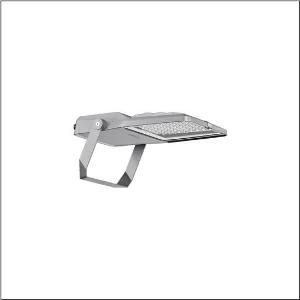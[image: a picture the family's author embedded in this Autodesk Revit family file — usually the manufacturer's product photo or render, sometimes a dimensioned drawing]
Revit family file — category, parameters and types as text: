
# Revit family: floodlight_fl_21_mini___pl52_5xa7775d2d1a_5239
name_source: partatom
category: Lighting Fixtures
units: mm (PartAtom-declared; Revit-internal decimal feet)

## family parameters
Cut with Voids When Loaded = No
Host = Face
Light Source = No
Part Type = Normal
Room Calculation Point = No
Round Connector Dimension = Use Diameter
Shared = No

## types (1)
- --- (1 x LED, 17840 lm, 142.9 W, 3000K)
    Apparent Load = 143 VA
    CIE Flux Codes = 26 60 98 100 100
    Color Rendering = 70
    Color Temperature = 3000K
    Default Elevation = 1800 mm
    Description = Floodlight FL 21 mini, floodlight, primary light control with lens, of PMMA, primary optical cover: protective disc, of toughened safety glass, transparent, light distribution: PL52, light emission: direct distribution, installation type: surface-mounted, LED, High Power LED, rated luminous flux: 17.840lm, luminous efficacy: 125lm/W, light colour: 730, colour temperature: 3000K, control gear: Smart Interface (Zhaga), control: flexible luminous flux parameterisation, time-dependent luminous flux control, constant luminous flux control, overheat protection, pre-setting: logarithmic dimming characteristic, with terminal, 6-pole, mains connection: 220..240V, AC, 50/60Hz, start of lifetime: 143W, end of service life: 151W, reduction: 63W, luminaire housing, of diecast aluminium, powder-coated, SITECO metallic grey (DB 702S), corrosivity category C5 mid according to DIN EN ISO 12944, suitable for swimming pools, chlorine-resistant, sealing non-destructively replaceable, mounting bracket, of steel, galvanised, powder-coated, SITECO metallic grey (DB 702S), Smart Interface above, protection rating (complete): IP66, insulation class (complete): insulation class II (safety insulation), certification: CE, ENEC, VDE, protection symbol: D, impact resistance: IK08, permissible operating ambient temperature: -40..+40°C, permissible operating ambient temperature for outdoor applications: -40..+50°C, standard: DIN EN 12944, LABS conformity tested according to VDMA 24364:2018-05, packaging unit: 1 piece

Light Distribution: PL52
    Height = 70 mm
    Lamp = 1 x LED
    Lamp Light Flux = 17840 lm
    Lamp Power = 142.9 W
    Lamp count = 1
    Length = 485 mm
    Luminous efficacy = 125 lm/W
    Manufacturer = Siteco
    ModVariant = No
    Model = 5XA7775D2D1A
    Mounting Place = Pole
    Mounting Type = Pole annexe
    Number of Poles = 1
    OnlyDefault = Yes
    Power Factor = 1
    Product Name = Floodlight FL 21 mini | PL52
    Product group = floodlight | pylon annexe
    ProductGroupID = 6201
    Protection Class = Protection class II
    Protection Degree = IP 66
    RLX_Detail_Level = 1
    RLX_Emergency_Light_Flux = 0 lm
    RLX_Emergency_Type = 0
    RLX_Emergency_Type_DB = No
    RlxData = <blob elided: 96525 chars, md5=0b63ff5b>
    Socket = socket
    Standby Power = 0 W
    System Light Flux = 17840 lm
    System Power = 143 W
    Type Comments = factory setting: luminous flux: 100 % | dim-lin: 254 | 730 mA
    Type Image = l_1006845.jpg
    URL = http://relux.com
    VarID = @adj_164239
    Voltage = 0 V
    Weight = 0.00 kg
    Width = 337 mm

## geometry (parser evidence)
native form markers: Blend x4, Sweep x13
no freeform markers — native parametric forms only
